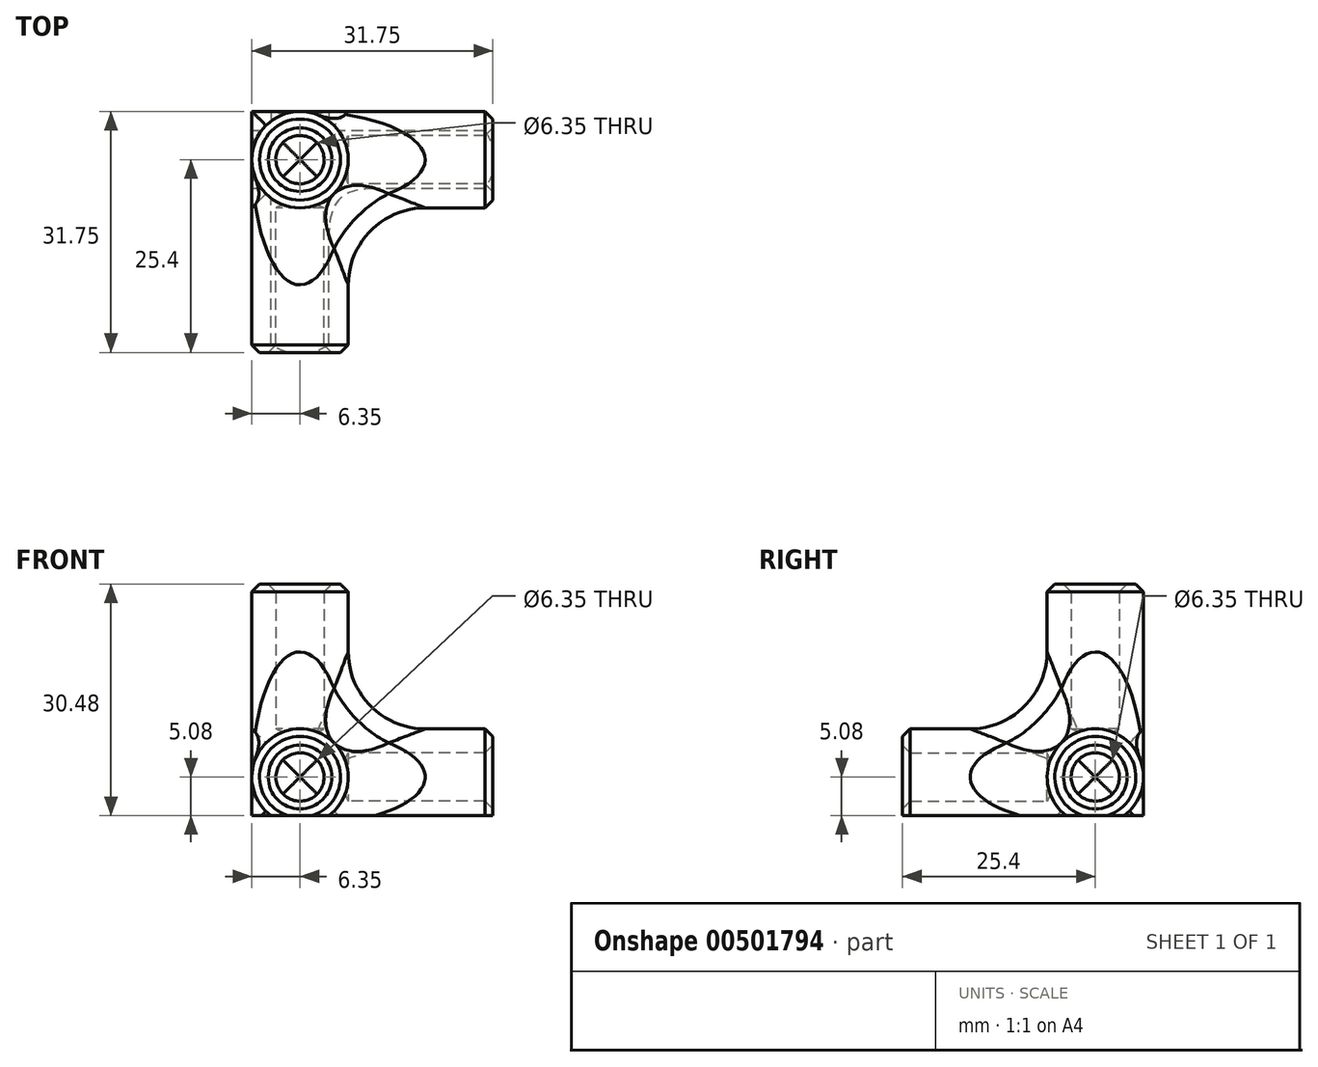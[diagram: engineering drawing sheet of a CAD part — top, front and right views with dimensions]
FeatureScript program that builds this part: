
annotation { "Feature Type Name" : "Feature", "Feature Type Description" : "" }
export const myFeature = defineFeature(function(context is Context, id is Id, definition is map)
    precondition{}
    {
        {
            var Q0;
            Q0=qCreatedBy(makeId("Top.planeOp"),FACE);
            var sketch = newSketch(context, id + "F0", { "sketchPlane" : qUnion([Q0])});
            skCircle(sketch, "E0", {"center": v(0, 0) * mm, "radius": 3.18 * mm});
            skCircle(sketch, "E1", {"center": v(0, 0) * mm, "radius": 6.35 * mm});
            skSolve(sketch);
        }
        {
            var Q0;
            Q0=makeQuery(id+"F0.imprint","IMPRINT",FACE,{"disambiguationData":[TD([[makeQuery(id+"F0.imprint","IMPRINT",EDGE,{"derivedFrom":sQuery(id+"F0.wireOp",EDGE,"E0")}),-1.0]])]});
            extrude(context, id + "F1", {"entities" : qUnion([Q0]), "depth" : 25.4 * mm});
        }
        {
            var Q0;
            Q0=qCreatedBy(makeId("Right.planeOp"),FACE);
            var sketch = newSketch(context, id + "F2", { "sketchPlane" : qUnion([Q0])});
            skCircle(sketch, "E2", {"center": v(0, 0) * mm, "radius": 6.35 * mm});
            skCircle(sketch, "E3", {"center": v(0, 0) * mm, "radius": 3.18 * mm});
            skSolve(sketch);
        }
        {
            var Q0;
            Q0=makeQuery(id+"F2.imprint","IMPRINT",FACE,{"disambiguationData":[TD([[makeQuery(id+"F2.imprint","IMPRINT",EDGE,{"derivedFrom":sQuery(id+"F2.wireOp",EDGE,"E2")}),1.0]])]});
            extrude(context, id + "F3", {"entities" : qUnion([Q0]), "operationType" : NewBodyOperationType.ADD, "depth" : 25.4 * mm});
        }
        {
            var Q0;
            Q0=qCreatedBy(makeId("Front.planeOp"),FACE);
            var sketch = newSketch(context, id + "F4", { "sketchPlane" : qUnion([Q0])});
            skCircle(sketch, "E4", {"center": v(0, 0) * mm, "radius": 3.18 * mm});
            skCircle(sketch, "E5", {"center": v(0, 0) * mm, "radius": 6.35 * mm});
            skSolve(sketch);
        }
        {
            var Q0;
            Q0=makeQuery(id+"F4.imprint","IMPRINT",FACE,{"disambiguationData":[TD([[makeQuery(id+"F4.imprint","IMPRINT",EDGE,{"derivedFrom":sQuery(id+"F4.wireOp",EDGE,"E4")}),-1.0]])]});
            extrude(context, id + "F5", {"entities" : qUnion([Q0]), "operationType" : NewBodyOperationType.ADD, "depth" : 25.4 * mm});
        }
        {
            var Q0;
            Q0 = qSketchRegion(id + "F2", true);
            extrude(context, id + "F6", {"entities" : qUnion([Q0]), "operationType" : NewBodyOperationType.ADD, "oppositeDirection" : true, "depth" : 6.35 * mm});
        }
        {
            var Q0;
            Q0 = qSketchRegion(id + "F0", true);
            extrude(context, id + "F7", {"entities" : qUnion([Q0]), "operationType" : NewBodyOperationType.ADD, "oppositeDirection" : true, "depth" : 6.35 * mm});
        }
        {
            var Q0;
            Q0 = qSketchRegion(id + "F4", true);
            extrude(context, id + "F8", {"entities" : qUnion([Q0]), "operationType" : NewBodyOperationType.ADD, "oppositeDirection" : true, "depth" : 6.35 * mm});
        }
        {
            var Q0;
            Q0=makeQuery(id+"F7.opExtrude","CAP_FACE",FACE,{"disambiguationData":[OSD([sQuery(id+"F0.wireOp",EDGE,"E0"),sQuery(id+"F0.wireOp",EDGE,"E1")])],"isStart":false});
            var sketch = newSketch(context, id + "F9", { "sketchPlane" : qUnion([Q0])});
            skSolve(sketch);
        }
        {
            var Q0;
            {var subQ0=sQuery(id+"F0.wireOp",EDGE,"E0");var subQ1=makeQuery(id+"F7.opExtrude","SWEPT_FACE",FACE,{"disambiguationData":[OSD([subQ0])]});var subQ2=sQuery(id+"F2.wireOp",EDGE,"E2");var subQ3=makeQuery(id+"F6.opExtrude","SWEPT_FACE",FACE,{"disambiguationData":[OSD([subQ2])]});var subQ6=makeQuery(id+"F3.opExtrude","SWEPT_FACE",FACE,{"disambiguationData":[OSD([subQ2])]});var subQ7=sQuery(id+"F0.wireOp",EDGE,"E1");var subQ8=makeQuery(id+"F7.opExtrude","CAP_FACE",FACE,{"disambiguationData":[OSD([subQ0,subQ7])],"isStart":false});var subQ9=makeQuery(id+"F7.opExtrude","CAP_EDGE",EDGE,{"disambiguationData":[OSD([subQ0])],"isStart":false});var subQ13=makeQuery(id+"F7.boolean.opBoolean","SPLIT",EDGE,{"disambiguationData":[TD([subQ6,subQ3,subQ1,subQ8])],"derivedFrom":subQ9});Q0=makeQuery(id+"F9.imprint","IMPRINT",FACE,{"disambiguationData":[TD([[makeQuery(id+"F9.imprint","IMPRINT",EDGE,{"derivedFrom":makeQuery(id+"F8.boolean.opBoolean","SPLIT",EDGE,{"disambiguationData":[OD(0.0)],"derivedFrom":subQ13})}),1.0]])]});}
            var sketch = newSketch(context, id + "F10", { "sketchPlane" : qUnion([Q0])});
            skLineSegment(sketch, "E6.bottom", {"start": v(-7.77, 27.78) * mm, "end": v(26.8, 27.78) * mm});
            skLineSegment(sketch, "E6.top", {"start": v(-7.77, -8.22) * mm, "end": v(26.8, -8.22) * mm});
            skLineSegment(sketch, "E6.left", {"start": v(-7.77, 27.78) * mm, "end": v(-7.77, -8.22) * mm});
            skLineSegment(sketch, "E6.right", {"start": v(26.8, 27.78) * mm, "end": v(26.8, -8.22) * mm});
            skSolve(sketch);
        }
        {
            var Q0;
            Q0 = qSketchRegion(id + "F10", true);
            extrude(context, id + "F11", {"entities" : qUnion([Q0]), "operationType" : NewBodyOperationType.REMOVE, "oppositeDirection" : true, "depth" : 1.27 * mm});
        }
        {
            var Q0;
            {var subQ0=sQuery(id+"F2.wireOp",EDGE,"E2");var subQ1=sQuery(id+"F0.wireOp",EDGE,"E1");var subQ2=makeQuery(id+"F1.opExtrude","SWEPT_FACE",FACE,{"disambiguationData":[OSD([subQ1])]});var subQ3=makeQuery(id+"F5.opExtrude","SWEPT_FACE",FACE,{"disambiguationData":[OSD([sQuery(id+"F4.wireOp",EDGE,"E5")])]});var subQ4=makeQuery(id+"F3.opExtrude","SWEPT_FACE",FACE,{"disambiguationData":[OSD([subQ0])]});Q0=makeQuery(id+"F7.boolean.opBoolean","SPLIT",EDGE,{"disambiguationData":[TD([subQ2])],"derivedFrom":makeQuery(id+"F5.boolean.opBoolean","INTERSECT",EDGE,{"derivedFrom":[makeQuery(id+"F3.boolean.opBoolean","SPLIT",FACE,{"disambiguationData":[TD([subQ2])],"derivedFrom":subQ4}),subQ3]})});}
            var Q1;
            {var subQ0=sQuery(id+"F0.wireOp",EDGE,"E1");var subQ1=makeQuery(id+"F1.opExtrude","SWEPT_FACE",FACE,{"disambiguationData":[OSD([subQ0])]});var subQ2=sQuery(id+"F2.wireOp",EDGE,"E2");var subQ3=makeQuery(id+"F3.opExtrude","SWEPT_FACE",FACE,{"disambiguationData":[OSD([subQ2])]});var subQ4=makeQuery(id+"F5.opExtrude","SWEPT_FACE",FACE,{"disambiguationData":[OSD([sQuery(id+"F4.wireOp",EDGE,"E5")])]});Q1=makeQuery(id+"F6.boolean.opBoolean","SPLIT",EDGE,{"disambiguationData":[TD([subQ3])],"derivedFrom":makeQuery(id+"F5.boolean.opBoolean","INTERSECT",EDGE,{"derivedFrom":[makeQuery(id+"F3.boolean.opBoolean","SPLIT",FACE,{"disambiguationData":[TD([subQ3])],"derivedFrom":subQ1}),subQ4]})});}
            var Q2;
            {var subQ0=sQuery(id+"F2.wireOp",EDGE,"E2");var subQ1=sQuery(id+"F0.wireOp",EDGE,"E1");var subQ2=makeQuery(id+"F1.opExtrude","SWEPT_FACE",FACE,{"disambiguationData":[OSD([subQ1])]});var subQ3=sQuery(id+"F4.wireOp",EDGE,"E5");var subQ4=makeQuery(id+"F5.opExtrude","SWEPT_FACE",FACE,{"disambiguationData":[OSD([subQ3])]});var subQ5=makeQuery(id+"F3.opExtrude","SWEPT_FACE",FACE,{"disambiguationData":[OSD([subQ0])]});Q2=makeQuery(id+"F8.boolean.opBoolean","SPLIT",EDGE,{"disambiguationData":[TD([subQ4])],"derivedFrom":makeQuery(id+"F5.boolean.opBoolean","SPLIT",EDGE,{"disambiguationData":[TD([subQ4])],"derivedFrom":makeQuery(id+"F3.boolean.opBoolean","INTERSECT",EDGE,{"derivedFrom":[subQ2,subQ5]})})});}
            fillet(context, id + "F12", {"entities" : qUnion([Q0, Q1, Q2]), "radius" : 10.16 * mm, "tangentPropagation" : true, "allowEdgeOverflow" : false});
        }
        {
            var Q0;
            Q0=makeQuery(id+"F5.opExtrude","CAP_EDGE",EDGE,{"disambiguationData":[OSD([sQuery(id+"F4.wireOp",EDGE,"E4")])],"isStart":false});
            var Q1;
            Q1=makeQuery(id+"F5.opExtrude","CAP_EDGE",EDGE,{"disambiguationData":[OSD([sQuery(id+"F4.wireOp",EDGE,"E5")])],"isStart":false});
            var Q2;
            Q2=makeQuery(id+"F1.opExtrude","CAP_EDGE",EDGE,{"disambiguationData":[OSD([sQuery(id+"F0.wireOp",EDGE,"E1")])],"isStart":false});
            var Q3;
            Q3=makeQuery(id+"F1.opExtrude","CAP_EDGE",EDGE,{"disambiguationData":[OSD([sQuery(id+"F0.wireOp",EDGE,"E0")])],"isStart":false});
            var Q4;
            Q4=makeQuery(id+"F3.opExtrude","CAP_EDGE",EDGE,{"disambiguationData":[OSD([sQuery(id+"F2.wireOp",EDGE,"E2")])],"isStart":false});
            var Q5;
            Q5=makeQuery(id+"F3.opExtrude","CAP_EDGE",EDGE,{"disambiguationData":[OSD([sQuery(id+"F2.wireOp",EDGE,"E3")])],"isStart":false});
            chamfer(context, id + "F13", {"entities" : qUnion([Q0, Q1, Q2, Q3, Q4, Q5]), "width" : 1.02 * mm, "tangentPropagation" : true});
        }
    });
